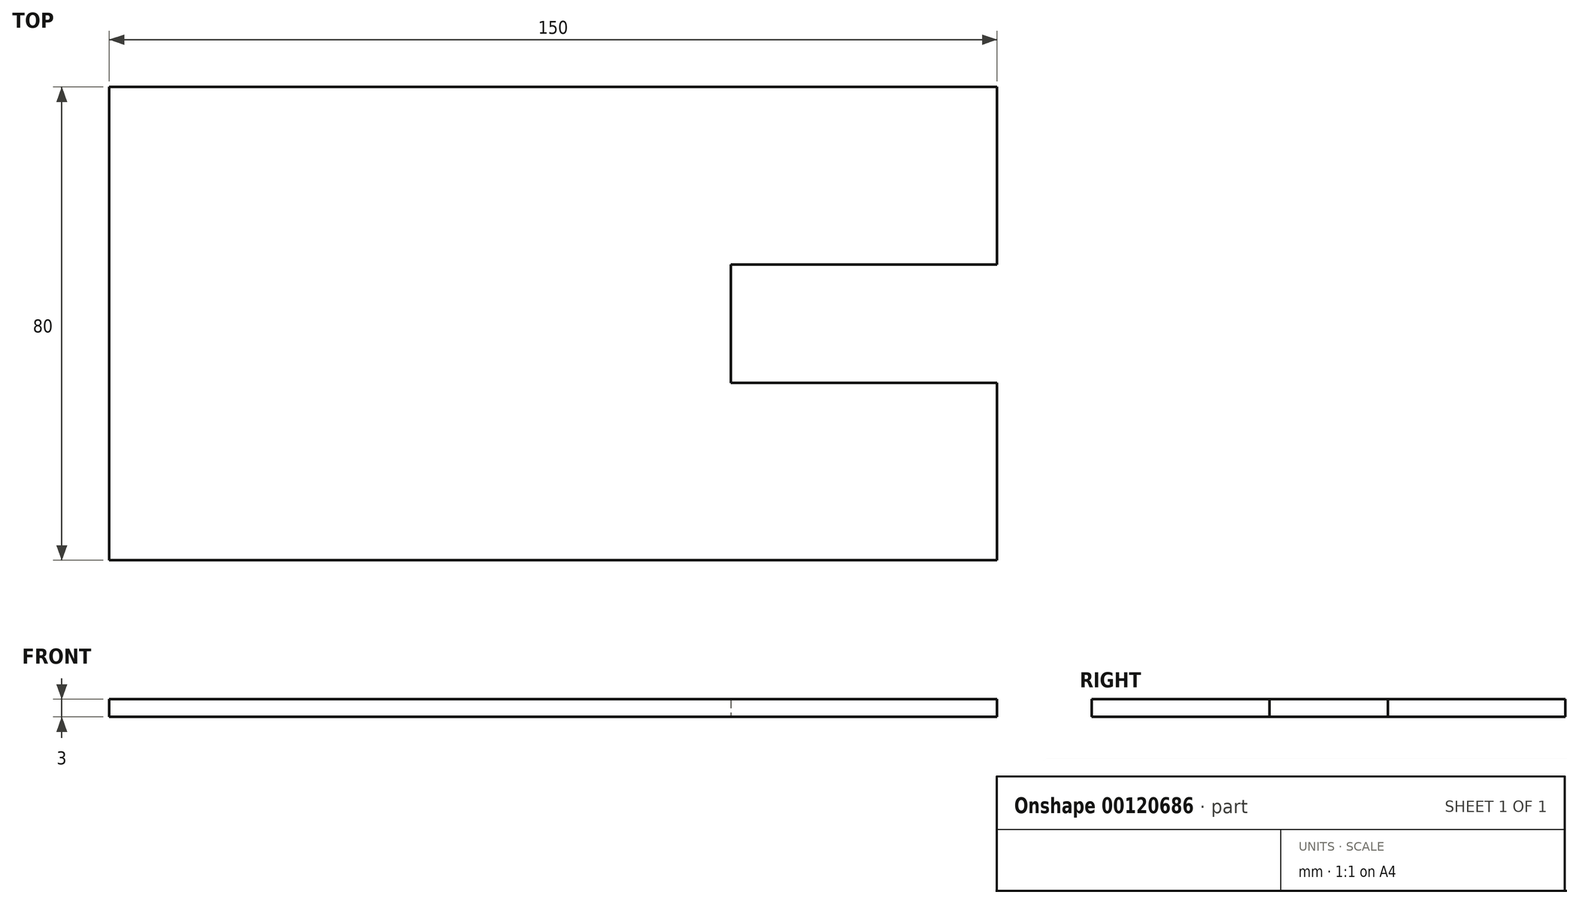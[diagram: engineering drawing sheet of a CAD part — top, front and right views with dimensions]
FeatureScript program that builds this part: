
annotation { "Feature Type Name" : "Feature", "Feature Type Description" : "" }
export const myFeature = defineFeature(function(context is Context, id is Id, definition is map)
    precondition{}
    {
        {
            var Q0;
            Q0=qCreatedBy(makeId("Top.planeOp"),FACE);
            var sketch = newSketch(context, id + "F0", { "sketchPlane" : qUnion([Q0])});
            skLineSegment(sketch, "E0.bottom", {"start": v(-94.9, 38.84) * mm, "end": v(55.1, 38.84) * mm});
            skLineSegment(sketch, "E0.top", {"start": v(-94.9, -41.16) * mm, "end": v(55.1, -41.16) * mm});
            skLineSegment(sketch, "E0.left", {"start": v(-94.9, 38.84) * mm, "end": v(-94.9, -41.16) * mm});
            skLineSegment(sketch, "E1", {"start": v(55.1, -11.16) * mm, "end": v(10.1, -11.16) * mm});
            skLineSegment(sketch, "E2", {"start": v(10.1, -11.16) * mm, "end": v(10.1, 8.84) * mm});
            skLineSegment(sketch, "E3", {"start": v(10.1, 8.84) * mm, "end": v(55.1, 8.84) * mm});
            skLineSegment(sketch, "E4", {"start": v(55.1, -41.16) * mm, "end": v(55.1, -11.16) * mm});
            skLineSegment(sketch, "E5", {"start": v(55.1, 8.84) * mm, "end": v(55.1, 38.84) * mm});
            skSolve(sketch);
        }
        {
            var Q0;
            Q0 = qSketchRegion(id + "F0", true);
            extrude(context, id + "F1", {"entities" : qUnion([Q0]), "depth" : 3 * mm});
        }
    });
